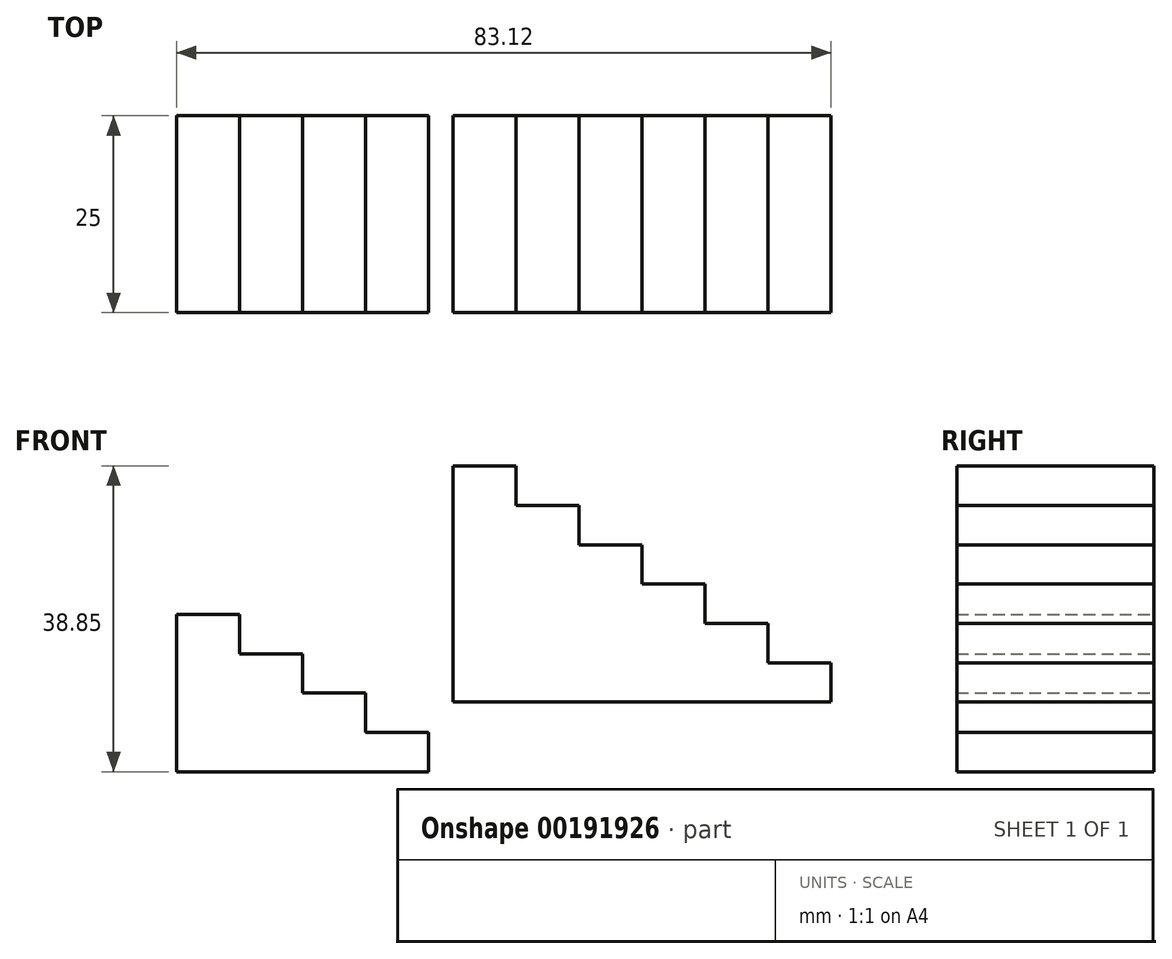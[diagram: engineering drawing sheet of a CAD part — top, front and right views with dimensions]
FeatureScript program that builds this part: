
annotation { "Feature Type Name" : "Feature", "Feature Type Description" : "" }
export const myFeature = defineFeature(function(context is Context, id is Id, definition is map)
    precondition{}
    {
        {
            var Q0;
            Q0=qCreatedBy(makeId("Front.planeOp"),FACE);
            var sketch = newSketch(context, id + "F0", { "sketchPlane" : qUnion([Q0])});
            skLineSegment(sketch, "E0", {"start": v(-7.45, 1.2) * mm, "end": v(-7.45, 21.2) * mm});
            skLineSegment(sketch, "E1", {"start": v(-7.45, 21.2) * mm, "end": v(0.55, 21.2) * mm});
            skLineSegment(sketch, "E2", {"start": v(0.55, 21.2) * mm, "end": v(0.55, 16.2) * mm});
            skLineSegment(sketch, "E3", {"start": v(0.55, 16.2) * mm, "end": v(8.55, 16.2) * mm});
            skLineSegment(sketch, "E4", {"start": v(8.55, 16.2) * mm, "end": v(8.55, 11.2) * mm});
            skLineSegment(sketch, "E5", {"start": v(8.55, 11.2) * mm, "end": v(16.55, 11.2) * mm});
            skLineSegment(sketch, "E6", {"start": v(16.55, 11.2) * mm, "end": v(16.55, 6.2) * mm});
            skLineSegment(sketch, "E7", {"start": v(16.55, 6.2) * mm, "end": v(24.55, 6.2) * mm});
            skLineSegment(sketch, "E8", {"start": v(24.55, 6.2) * mm, "end": v(24.55, 1.2) * mm});
            skLineSegment(sketch, "E9", {"start": v(24.55, 1.2) * mm, "end": v(-7.45, 1.2) * mm});
            skSolve(sketch);
        }
        {
            var Q0;
            Q0 = qSketchRegion(id + "F0", true);
            extrude(context, id + "F1", {"entities" : qUnion([Q0]), "depth" : 25 * mm});
        }
        {
            var Q0;
            Q0=qCreatedBy(makeId("Front.planeOp"),FACE);
            var sketch = newSketch(context, id + "F2", { "sketchPlane" : qUnion([Q0])});
            skLineSegment(sketch, "E10", {"start": v(27.67, 10.05) * mm, "end": v(27.67, 40.05) * mm});
            skLineSegment(sketch, "E11", {"start": v(27.67, 40.05) * mm, "end": v(35.67, 40.05) * mm});
            skLineSegment(sketch, "E12", {"start": v(35.67, 40.05) * mm, "end": v(35.67, 35.05) * mm});
            skLineSegment(sketch, "E13", {"start": v(35.67, 35.05) * mm, "end": v(43.67, 35.05) * mm});
            skLineSegment(sketch, "E14", {"start": v(43.67, 35.05) * mm, "end": v(43.67, 30.05) * mm});
            skLineSegment(sketch, "E15", {"start": v(43.67, 30.05) * mm, "end": v(51.67, 30.05) * mm});
            skLineSegment(sketch, "E16", {"start": v(51.67, 30.05) * mm, "end": v(51.67, 25.05) * mm});
            skLineSegment(sketch, "E17", {"start": v(51.67, 25.05) * mm, "end": v(59.67, 25.05) * mm});
            skLineSegment(sketch, "E18", {"start": v(59.67, 25.05) * mm, "end": v(59.67, 20.05) * mm});
            skLineSegment(sketch, "E19", {"start": v(59.67, 20.05) * mm, "end": v(67.67, 20.05) * mm});
            skLineSegment(sketch, "E20", {"start": v(67.67, 20.05) * mm, "end": v(67.67, 15.05) * mm});
            skLineSegment(sketch, "E21", {"start": v(67.67, 15.05) * mm, "end": v(75.67, 15.05) * mm});
            skLineSegment(sketch, "E22", {"start": v(75.67, 15.05) * mm, "end": v(75.67, 10.05) * mm});
            skLineSegment(sketch, "E23", {"start": v(75.67, 10.05) * mm, "end": v(28.95, 10.05) * mm});
            skLineSegment(sketch, "E24", {"start": v(28.95, 10.05) * mm, "end": v(27.67, 10.05) * mm});
            skSolve(sketch);
        }
        {
            var Q0;
            Q0 = qSketchRegion(id + "F2", true);
            extrude(context, id + "F3", {"entities" : qUnion([Q0]), "depth" : 25 * mm});
        }
    });
